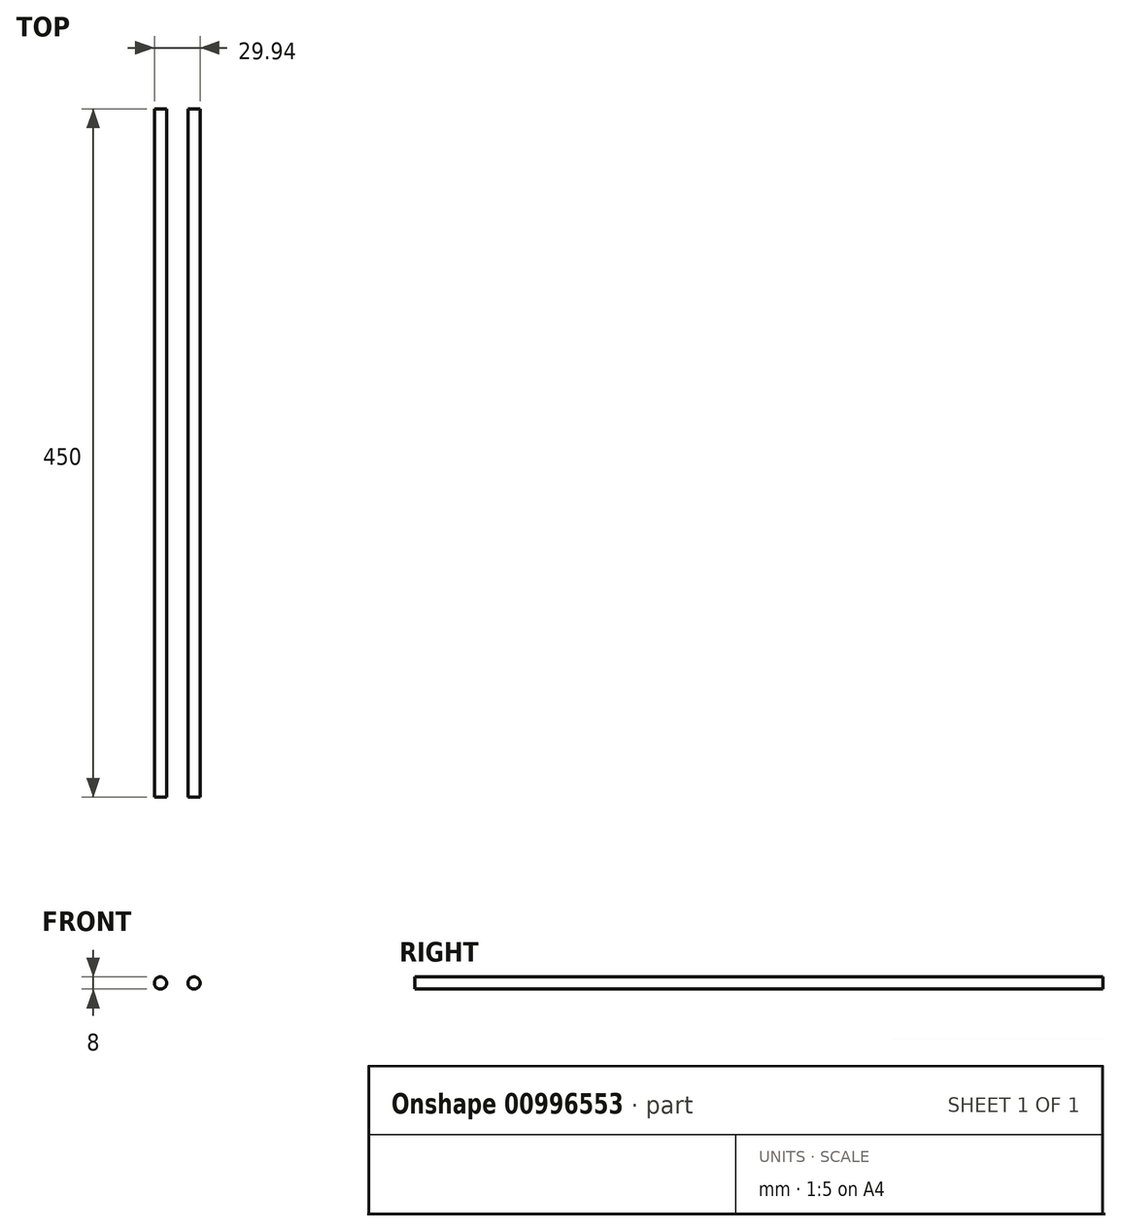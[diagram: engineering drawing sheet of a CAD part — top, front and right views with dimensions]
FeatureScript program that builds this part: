
annotation { "Feature Type Name" : "Feature", "Feature Type Description" : "" }
export const myFeature = defineFeature(function(context is Context, id is Id, definition is map)
    precondition{}
    {
        {
            var Q0;
            Q0=qCreatedBy(makeId("Front.planeOp"),FACE);
            var sketch = newSketch(context, id + "F0", { "sketchPlane" : qUnion([Q0])});
            skCircle(sketch, "E0", {"center": v(-37.36, 10.28) * mm, "radius": 4 * mm});
            skCircle(sketch, "E1", {"center": v(-15.42, 10.28) * mm, "radius": 4 * mm});
            skSolve(sketch);
        }
        {
            assignVariable(context, id + "F1", {"name" : "xRodLength", "anyValue" : 450});
        }
        {
            assignVariable(context, id + "F2", {"name" : "yRodLength", "anyValue" : 450});
        }
        {
            var Q0;
            Q0=makeQuery(id+"F0.imprint","IMPRINT",FACE,{"disambiguationData":[TD([[makeQuery(id+"F0.imprint","IMPRINT",EDGE,{"derivedFrom":sQuery(id+"F0.wireOp",EDGE,"E0")}),1.0]])]});
            extrude(context, id + "F3", {"entities" : qUnion([Q0]), "depth" : (getVariable(context, 'xRodLength')) * mm, "offsetDistance" : 25 * mm});
        }
        {
            var Q0;
            Q0=makeQuery(id+"F0.imprint","IMPRINT",FACE,{"disambiguationData":[TD([[makeQuery(id+"F0.imprint","IMPRINT",EDGE,{"derivedFrom":sQuery(id+"F0.wireOp",EDGE,"E1")}),1.0]])]});
            extrude(context, id + "F4", {"entities" : qUnion([Q0]), "depth" : (getVariable(context, 'yRodLength')) * mm, "offsetDistance" : 25 * mm});
        }
    });
